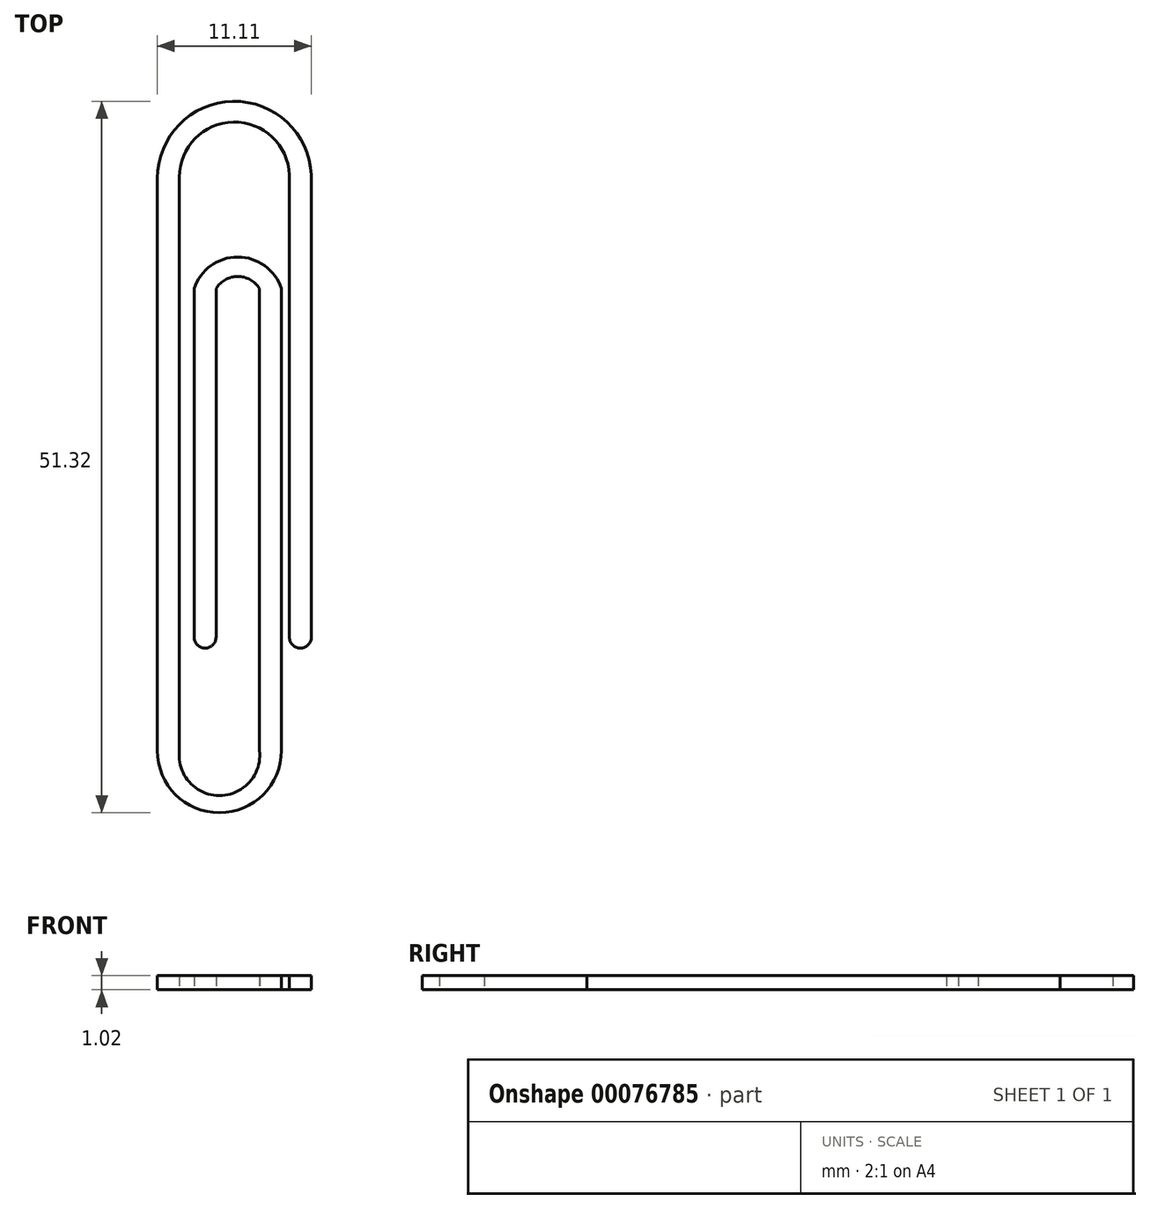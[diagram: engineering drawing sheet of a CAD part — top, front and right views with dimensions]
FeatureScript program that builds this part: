
annotation { "Feature Type Name" : "Feature", "Feature Type Description" : "" }
export const myFeature = defineFeature(function(context is Context, id is Id, definition is map)
    precondition{}
    {
        {
            var Q0;
            Q0=qCreatedBy(makeId("Top.planeOp"),FACE);
            var sketch = newSketch(context, id + "F0", { "sketchPlane" : qUnion([Q0])});
            skLineSegment(sketch, "E0", {"start": v(-19.76, 13.62) * mm, "end": v(-19.76, -27.66) * mm});
            skLineSegment(sketch, "E1", {"start": v(-18.17, 13.72) * mm, "end": v(-18.17, -27.66) * mm});
            skLineSegment(sketch, "E2", {"start": v(-10.23, 13.87) * mm, "end": v(-10.23, -19.47) * mm});
            skLineSegment(sketch, "E3", {"start": v(-8.65, 13.87) * mm, "end": v(-8.65, -19.47) * mm});
            skArc(sketch, "E4", {"start": v(-8.65, 13.87) * mm, "mid": v(-14.32, 19.17) * mm, "end": v(-19.76, 13.62) * mm});
            skArc(sketch, "E5", {"start": v(-10.23, 13.87) * mm, "mid": v(-14.28, 17.69) * mm, "end": v(-18.17, 13.72) * mm});
            skArc(sketch, "E6", {"start": v(-10.23, -19.47) * mm, "mid": v(-9.44, -20.26) * mm, "end": v(-8.65, -19.47) * mm});
            skLineSegment(sketch, "E7", {"start": v(-10.8, -27.66) * mm, "end": v(-10.8, 5.68) * mm});
            skLineSegment(sketch, "E8", {"start": v(-12.4, 5.68) * mm, "end": v(-12.4, -27.66) * mm});
            skLineSegment(sketch, "E9", {"start": v(-17.11, -19.47) * mm, "end": v(-17.11, 5.68) * mm});
            skLineSegment(sketch, "E10", {"start": v(-15.52, -19.47) * mm, "end": v(-15.52, 5.68) * mm});
            skArc(sketch, "E11", {"start": v(-10.8, 5.68) * mm, "mid": v(-13.96, 7.95) * mm, "end": v(-17.11, 5.68) * mm});
            skArc(sketch, "E12", {"start": v(-12.4, 5.68) * mm, "mid": v(-13.96, 6.55) * mm, "end": v(-15.52, 5.68) * mm});
            skArc(sketch, "E13", {"start": v(-17.11, -19.47) * mm, "mid": v(-16.32, -20.26) * mm, "end": v(-15.52, -19.47) * mm});
            skArc(sketch, "E14", {"start": v(-19.76, -27.66) * mm, "mid": v(-15.28, -32.14) * mm, "end": v(-10.8, -27.66) * mm});
            skArc(sketch, "E15", {"start": v(-18.17, -27.66) * mm, "mid": v(-15.28, -30.9) * mm, "end": v(-12.4, -27.66) * mm});
            skSolve(sketch);
        }
        {
            var Q0;
            Q0=makeQuery(id+"F0.imprint","IMPRINT",FACE,{"disambiguationData":[TD([[makeQuery(id+"F0.imprint","IMPRINT",EDGE,{"derivedFrom":sQuery(id+"F0.wireOp",EDGE,"E0")}),1.0]])]});
            extrude(context, id + "F1", {"entities" : qUnion([Q0]), "depth" : 1.02 * mm});
        }
    });
